# Revit family: HQ
name_source: partatom
category: Pipe Accessories
revit_build: Autodesk Revit 2017 (Build: 20160225_1515(x64)
units: mm (PartAtom-declared; Revit-internal decimal feet)

## family parameters
Always vertical = Yes
Cut with Voids When Loaded = Yes
OmniClass Number = 23.27.31.27
OmniClass Title = Globe Valves
Part Type = Valve - Normal
Round Connector Dimension = Use Diameter
Shared = Yes
Work Plane-Based = No

## types (3) — shared parameters
Assembly Code = G2050700
Body Material = Hunter® Red Brass and Staineless Steel
Height = 13 mm
Inner Diameter = 25 mm  [stored 0.082021 ft]
Keynote = 328423.01
Length = 84 mm  [stored 0.275591 ft]
Loss Method = Not Defined
Manufacturer = Hunter® Industries
Outer Diameter = 32 mm  [stored 0.104987 ft]
Pipe Diameter = 25 mm  [stored 0.082021 ft]
Show Valve Box = Yes
Type Comments = Quick Coupler
Type Image = <None>
URL = https://www.hunterindustries.com
Width = 84 mm  [stored 0.275591 ft]
zero-valued in all types: K Coefficient

## per-type parameters (varying)
| type | Description | Flow | Flow_Value | HQ body | Inlet Diameter | Max_Flow | Min_Flow | Model | Model_Ref | Operating Flow | Pressure Loss | Tag Name |
| HQ-33DLRC | HQ33D Valve with locking rubber cover | 75.7 L/min | 75.7 | HQ33 | 3/4" (20mm) | 75.7 L/min | 18.9 L/min | HQ-33DLRC | 33 | 75.7 L/min | 15.0 kPa | HQ-33DLRC |
| HQ-44LRC | HQ44D Valve with locking rubber cover | 100.0 L/min | 100 | HQ44 | 1" (25mm) NPT | 113.6 L/min | 56.8 L/min | HQ-44DLRC | 44 | 100.0 L/min | 15.0 kPa | HQ-44DLRC |
| HQ-5LRC | HQ5D Valve with locking rubber cover | 100.0 L/min | 100 | HQ5 | 1" (25mm) NPT | 265.0 L/min | 75.7 L/min | HQ-5DLRC | 5 | 100.0 L/min | 11.3 kPa | HQ-5DLRC |

note: [stored X ft] marks values corroborated as IEEE doubles in the binary element streams (Revit-internal decimal feet)

## geometry (parser evidence)
native form markers: Sweep x13
no freeform markers — native parametric forms only
